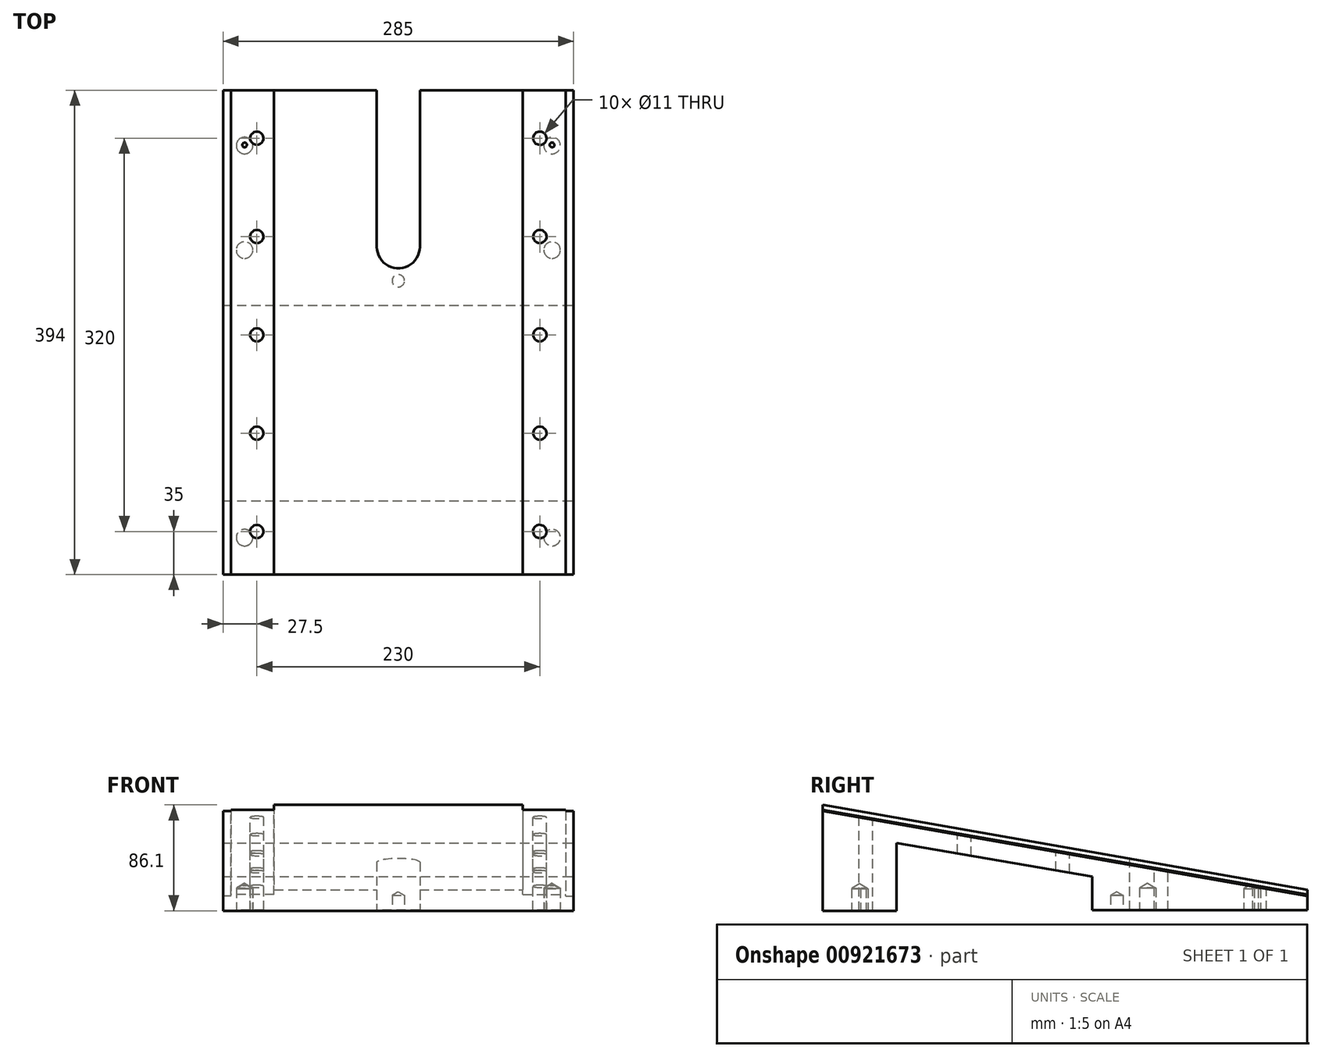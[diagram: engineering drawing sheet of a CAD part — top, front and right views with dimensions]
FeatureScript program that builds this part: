
annotation { "Feature Type Name" : "Feature", "Feature Type Description" : "" }
export const myFeature = defineFeature(function(context is Context, id is Id, definition is map)
    precondition{}
    {
        {
            var Q0;
            Q0=qCreatedBy(makeId("Right.planeOp"),FACE);
            var sketch = newSketch(context, id + "F0", { "sketchPlane" : qUnion([Q0])});
            skLineSegment(sketch, "E0", {"start": v(0, 86.1) * mm, "end": v(0, 65.8) * mm});
            skLineSegment(sketch, "E1", {"start": v(0, 65.8) * mm, "end": v(0, 0) * mm});
            skLineSegment(sketch, "E2", {"start": v(0, 0) * mm, "end": v(60, 0) * mm});
            skLineSegment(sketch, "E3", {"start": v(394, 0.48) * mm, "end": v(394, 17.08) * mm});
            skLineSegment(sketch, "E4", {"start": v(0, 86.1) * mm, "end": v(394, 17.08) * mm});
            skLineSegment(sketch, "E5", {"start": v(60, 0) * mm, "end": v(60, 55.2) * mm});
            skLineSegment(sketch, "E6", {"start": v(394, 0.48) * mm, "end": v(219, 0.48) * mm});
            skLineSegment(sketch, "E7", {"start": v(219, 0.48) * mm, "end": v(219, 27.68) * mm});
            skLineSegment(sketch, "E8", {"start": v(0, 65.8) * mm, "end": v(60, 55.2) * mm});
            skLineSegment(sketch, "E9", {"start": v(60, 55.2) * mm, "end": v(219, 27.68) * mm});
            skPoint(sketch, "E10.start.orphan", {"position": v(249, 0.48) * mm});
            skPoint(sketch, "E11", {"position": v(40.39, 79.03) * mm});
            skPoint(sketch, "E12", {"position": v(119.19, 65.22) * mm});
            skPoint(sketch, "E13", {"position": v(197.99, 51.42) * mm});
            skPoint(sketch, "E14", {"position": v(276.79, 37.61) * mm});
            skPoint(sketch, "E15", {"position": v(355.59, 23.8) * mm});
            skSolve(sketch);
        }
        {
            var Q0;
            {var subQ0=sQuery(id+"F0.wireOp",EDGE,"E1");Q0=makeQuery(id+"F0.imprint","IMPRINT",FACE,{"disambiguationData":[TD([[makeQuery(id+"F0.imprint","IMPRINT",EDGE,{"derivedFrom":subQ0}),1.0]])]});}
            var Q1;
            {var subQ3=sQuery(id+"F0.wireOp",EDGE,"E0");Q1=makeQuery(id+"F0.imprint","IMPRINT",FACE,{"disambiguationData":[TD([[makeQuery(id+"F0.imprint","IMPRINT",EDGE,{"derivedFrom":subQ3}),1.0]])]});}
            var Q2;
            {var subQ0=sQuery(id+"F0.wireOp",EDGE,"E7");Q2=makeQuery(id+"F0.imprint","IMPRINT",FACE,{"disambiguationData":[TD([[makeQuery(id+"F0.imprint","IMPRINT",EDGE,{"derivedFrom":subQ0}),-1.0]])]});}
            var Q3;
            {var subQ0=sQuery(id+"F0.wireOp",EDGE,"E6");var subQ1=sQuery(id+"F0.wireOp",EDGE,"0UA3Y2bc-zSIp-0L5M-hBtJ-KGsreEd9ITGh");var subQ2=makeQuery(id+"F0.imprint","INTERSECT",VERTEX,{"derivedFrom":[subQ1,subQ0]});Q3=makeQuery(id+"F0.imprint","IMPRINT",FACE,{"disambiguationData":[TD([[makeQuery(id+"F0.imprint","IMPRINT",EDGE,{"disambiguationData":[TD([[subQ2,1.0]])],"derivedFrom":subQ1}),-1.0]])]});}
            var Q4;
            {var subQ1=sQuery(id+"F0.wireOp",EDGE,"E3");Q4=makeQuery(id+"F0.imprint","IMPRINT",FACE,{"disambiguationData":[TD([[makeQuery(id+"F0.imprint","IMPRINT",EDGE,{"derivedFrom":subQ1}),1.0]])]});}
            extrude(context, id + "F1", {"entities" : qUnion([Q0, Q1, Q2, Q3, Q4]), "oppositeDirection" : true, "depth" : 285 * mm, "offsetDistance" : 25 * mm});
        }
        {
            var Q0;
            Q0=makeQuery(id+"F1.opExtrude","CAP_FACE",FACE,{"disambiguationData":[OSD([sQuery(id+"F0.wireOp",EDGE,"E0"),sQuery(id+"F0.wireOp",EDGE,"E1"),sQuery(id+"F0.wireOp",EDGE,"E2"),sQuery(id+"F0.wireOp",EDGE,"E3"),sQuery(id+"F0.wireOp",EDGE,"E4"),sQuery(id+"F0.wireOp",EDGE,"0UA3Y2bc-zSIp-0L5M-hBtJ-KGsreEd9ITGh"),sQuery(id+"F0.wireOp",EDGE,"E5"),sQuery(id+"F0.wireOp",EDGE,"E6"),sQuery(id+"F0.wireOp",EDGE,"E7")])],"isStart":true});
            var sketch = newSketch(context, id + "F2", { "sketchPlane" : qUnion([Q0])});
            skLineSegment(sketch, "E16", {"start": v(0, 86.1) * mm, "end": v(0, 82.1) * mm});
            skLineSegment(sketch, "E17", {"start": v(0, 82.1) * mm, "end": v(394, 13.08) * mm});
            skLineSegment(sketch, "E18", {"start": v(394, 13.08) * mm, "end": v(394, 17.08) * mm});
            skLineSegment(sketch, "E19", {"start": v(394, 17.08) * mm, "end": v(0, 86.1) * mm});
            skSolve(sketch);
        }
        {
            var Q0;
            Q0=makeQuery(id+"F2.imprint","IMPRINT",FACE,{"disambiguationData":[TD([[makeQuery(id+"F2.imprint","IMPRINT",EDGE,{"derivedFrom":sQuery(id+"F2.wireOp",EDGE,"E16")}),1.0]])]});
            extrude(context, id + "F3", {"entities" : qUnion([Q0]), "operationType" : NewBodyOperationType.REMOVE, "oppositeDirection" : true, "depth" : 41.5 * mm, "offsetDistance" : 25 * mm});
        }
        {
            var Q0;
            Q0=makeQuery(id+"F1.opExtrude","CAP_FACE",FACE,{"disambiguationData":[OSD([sQuery(id+"F0.wireOp",EDGE,"E0"),sQuery(id+"F0.wireOp",EDGE,"E1"),sQuery(id+"F0.wireOp",EDGE,"E2"),sQuery(id+"F0.wireOp",EDGE,"E3"),sQuery(id+"F0.wireOp",EDGE,"E4"),sQuery(id+"F0.wireOp",EDGE,"0UA3Y2bc-zSIp-0L5M-hBtJ-KGsreEd9ITGh"),sQuery(id+"F0.wireOp",EDGE,"E5"),sQuery(id+"F0.wireOp",EDGE,"E6"),sQuery(id+"F0.wireOp",EDGE,"E7")])],"isStart":true});
            var sketch = newSketch(context, id + "F4", { "sketchPlane" : qUnion([Q0])});
            skLineSegment(sketch, "E20", {"start": v(0, 82.1) * mm, "end": v(0, 81.1) * mm});
            skLineSegment(sketch, "E21", {"start": v(0, 81.1) * mm, "end": v(394, 12.08) * mm});
            skLineSegment(sketch, "E22", {"start": v(394, 12.08) * mm, "end": v(394, 13.08) * mm});
            skLineSegment(sketch, "E23", {"start": v(0, 82.1) * mm, "end": v(394, 13.08) * mm});
            skSolve(sketch);
        }
        {
            var Q0;
            Q0=makeQuery(id+"F4.imprint","IMPRINT",FACE,{"disambiguationData":[TD([[makeQuery(id+"F4.imprint","IMPRINT",EDGE,{"derivedFrom":sQuery(id+"F4.wireOp",EDGE,"E20")}),1.0]])]});
            extrude(context, id + "F5", {"entities" : qUnion([Q0]), "operationType" : NewBodyOperationType.REMOVE, "oppositeDirection" : true, "depth" : 6.5 * mm, "offsetDistance" : 25 * mm});
        }
        {
            var Q0;
            Q0=makeQuery(id+"F1.opExtrude","CAP_FACE",FACE,{"disambiguationData":[OSD([sQuery(id+"F0.wireOp",EDGE,"E0"),sQuery(id+"F0.wireOp",EDGE,"E1"),sQuery(id+"F0.wireOp",EDGE,"E2"),sQuery(id+"F0.wireOp",EDGE,"E3"),sQuery(id+"F0.wireOp",EDGE,"E4"),sQuery(id+"F0.wireOp",EDGE,"0UA3Y2bc-zSIp-0L5M-hBtJ-KGsreEd9ITGh"),sQuery(id+"F0.wireOp",EDGE,"E5"),sQuery(id+"F0.wireOp",EDGE,"E6"),sQuery(id+"F0.wireOp",EDGE,"E7")])],"isStart":false});
            var sketch = newSketch(context, id + "F6", { "sketchPlane" : qUnion([Q0])});
            skLineSegment(sketch, "E24", {"start": v(-394, 17.08) * mm, "end": v(-394, 13.08) * mm});
            skLineSegment(sketch, "E25", {"start": v(-394, 13.08) * mm, "end": v(-394, 12.08) * mm});
            skLineSegment(sketch, "E26", {"start": v(0, 86.1) * mm, "end": v(0, 82.1) * mm});
            skLineSegment(sketch, "E27", {"start": v(0, 82.1) * mm, "end": v(0, 81.1) * mm});
            skLineSegment(sketch, "E28", {"start": v(0, 86.1) * mm, "end": v(-394, 17.08) * mm});
            skLineSegment(sketch, "E29", {"start": v(-394, 13.08) * mm, "end": v(0, 82.1) * mm});
            skLineSegment(sketch, "E30", {"start": v(0, 81.1) * mm, "end": v(-394, 12.08) * mm});
            skSolve(sketch);
        }
        {
            var Q0;
            Q0=makeQuery(id+"F6.imprint","IMPRINT",FACE,{"disambiguationData":[TD([[makeQuery(id+"F6.imprint","IMPRINT",EDGE,{"derivedFrom":sQuery(id+"F6.wireOp",EDGE,"E24")}),-1.0]])]});
            extrude(context, id + "F7", {"entities" : qUnion([Q0]), "operationType" : NewBodyOperationType.REMOVE, "oppositeDirection" : true, "depth" : 41.5 * mm, "offsetDistance" : 25 * mm});
        }
        {
            var Q0;
            Q0=makeQuery(id+"F6.imprint","IMPRINT",FACE,{"disambiguationData":[TD([[makeQuery(id+"F6.imprint","IMPRINT",EDGE,{"derivedFrom":sQuery(id+"F6.wireOp",EDGE,"E25")}),-1.0]])]});
            extrude(context, id + "F8", {"entities" : qUnion([Q0]), "operationType" : NewBodyOperationType.REMOVE, "oppositeDirection" : true, "depth" : 6.5 * mm, "offsetDistance" : 25 * mm});
        }
        {
            var Q0;
            Q0=makeQuery(id+"F1.opExtrude","SWEPT_FACE",FACE,{"disambiguationData":[OSD([sQuery(id+"F0.wireOp",EDGE,"E4")])]});
            var sketch = newSketch(context, id + "F9", { "sketchPlane" : qUnion([Q0])});
            skSolve(sketch);
        }
        {
            var Q0;
            Q0=makeQuery(id+"F9.imprint","IMPRINT",FACE,{"disambiguationData":[TD([[makeQuery(id+"F9.imprint","IMPRINT",EDGE,{"derivedFrom":makeQuery(id+"F3.boolean.opBoolean","COPY",EDGE,{"derivedFrom":makeQuery(id+"F3.opExtrude","CAP_EDGE",EDGE,{"disambiguationData":[OSD([sQuery(id+"F2.wireOp",EDGE,"E19")])],"isStart":false})})}),1.0]])]});
            var sketch = newSketch(context, id + "F10", { "sketchPlane" : qUnion([Q0])});
            skSolve(sketch);
        }
        {
            var Q0;
            Q0=qCreatedBy(makeId("Top.planeOp"),FACE);
            cPlane(context, id + "F11", {"entities" : qUnion([Q0]), "cplaneType" : CPlaneType.OFFSET, "offset" : 86.1 * mm, "width" : 150 * mm, "height" : 150 * mm});
        }
        {
            var Q0;
            Q0=qCreatedBy(id+"F11.planeOp",FACE);
            var sketch = newSketch(context, id + "F12", { "sketchPlane" : qUnion([Q0])});
            skLineSegment(sketch, "E31", {"start": v(-257.5, 394) * mm, "end": v(-257.5, -6) * mm, "construction": true});
            skLineSegment(sketch, "E32", {"start": v(-27.5, 394) * mm, "end": v(-27.5, -70.85) * mm, "construction": true});
            skPoint(sketch, "E33", {"position": v(-257.5, 355) * mm});
            skPoint(sketch, "E34", {"position": v(-257.5, 275) * mm});
            skPoint(sketch, "E35", {"position": v(-257.5, 195) * mm});
            skPoint(sketch, "E36", {"position": v(-257.5, -6) * mm});
            skPoint(sketch, "E37", {"position": v(-27.5, 355) * mm});
            skPoint(sketch, "E38", {"position": v(-27.5, 275) * mm});
            skPoint(sketch, "E39", {"position": v(-27.5, 195) * mm});
            skPoint(sketch, "E40", {"position": v(-27.5, 115) * mm});
            skPoint(sketch, "E41", {"position": v(-27.5, 35) * mm});
            skLineSegment(sketch, "E42.0.0", {"start": v(-243.5, 394) * mm, "end": v(-278.5, 394) * mm});
            skLineSegment(sketch, "E42.0.1", {"start": v(-278.5, 394) * mm, "end": v(-278.5, 0) * mm});
            skLineSegment(sketch, "E42.0.2", {"start": v(-278.5, 0) * mm, "end": v(-243.5, 0) * mm});
            skLineSegment(sketch, "E42.0.3", {"start": v(-243.5, 0) * mm, "end": v(-243.5, 394) * mm});
            skPoint(sketch, "E43", {"position": v(-257.5, 115) * mm});
            skPoint(sketch, "E44", {"position": v(-257.5, 35) * mm});
            skLineSegment(sketch, "E45.0", {"start": v(-285, 0) * mm, "end": v(0, 0) * mm, "construction": true});
            skSolve(sketch);
        }
        {
            var Q0;
            Q0=sQuery(id+"F12.wireOp",VERTEX,"E33");
            var Q1;
            Q1=sQuery(id+"F12.wireOp",VERTEX,"E34");
            var Q2;
            Q2=sQuery(id+"F12.wireOp",VERTEX,"E35");
            var Q3;
            Q3=sQuery(id+"F12.wireOp",VERTEX,"E37");
            var Q4;
            Q4=sQuery(id+"F12.wireOp",VERTEX,"E38");
            var Q5;
            Q5=sQuery(id+"F12.wireOp",VERTEX,"E39");
            var Q6;
            Q6=sQuery(id+"F12.wireOp",VERTEX,"E40");
            var Q7;
            Q7=sQuery(id+"F12.wireOp",VERTEX,"E41");
            var Q8;
            Q8=sQuery(id+"F12.wireOp",VERTEX,"8ee47a5b-37d2-4881-83f4-5071e9de7b0a");
            var Q9;
            Q9=sQuery(id+"F12.wireOp",VERTEX,"E43");
            var Q10;
            Q10=sQuery(id+"F12.wireOp",VERTEX,"E44");
            var Q11;
            Q11=makeQuery(id+"F1.opExtrude","SWEPT_BODY",BODY,{"disambiguationData":[OSD([sQuery(id+"F0.wireOp",EDGE,"E0"),sQuery(id+"F0.wireOp",EDGE,"E1"),sQuery(id+"F0.wireOp",EDGE,"E2"),sQuery(id+"F0.wireOp",EDGE,"E3"),sQuery(id+"F0.wireOp",EDGE,"E4"),sQuery(id+"F0.wireOp",EDGE,"E5"),sQuery(id+"F0.wireOp",EDGE,"E6"),sQuery(id+"F0.wireOp",EDGE,"E7"),sQuery(id+"F0.wireOp",EDGE,"E9")])]});
            hole(context, id + "F13", {"style" : HoleStyle.SIMPLE, "endStyle" : HoleEndStyle.THROUGH, "standardTappedOrClearance" : lookupTablePath({ "fit" : "Normal", "standard" : "ISO", "size" : "M10", "type" : "Clearance" }), "standardBlindInLast" : lookupTablePath({ "fit" : "Normal", "standard" : "ISO", "size" : "M10", "type" : "Clearance" }), "holeDiameter" : 11 * mm, "majorDiameter" : 5 * mm, "isTappedThrough" : true, "tappedDepth" : 12 * mm, "tapClearance" : 3, "locations" : qUnion([Q0, Q1, Q2, Q3, Q4, Q5, Q6, Q7, Q8, Q9, Q10]), "scope" : qUnion([Q11])});
        }
        {
            var Q0;
            Q0=makeQuery(id+"F1.opExtrude","SWEPT_FACE",FACE,{"disambiguationData":[OSD([sQuery(id+"F0.wireOp",EDGE,"E2")])]});
            var sketch = newSketch(context, id + "F14", { "sketchPlane" : qUnion([Q0])});
            skLineSegment(sketch, "E46.0", {"start": v(-285, 0) * mm, "end": v(0, 0) * mm});
            skLineSegment(sketch, "E47", {"start": v(-142.5, 0) * mm, "end": v(-142.5, -475.57) * mm, "construction": true});
            skLineSegment(sketch, "E48", {"start": v(-142.5, 0) * mm, "end": v(-17.5, 0) * mm, "construction": true});
            skLineSegment(sketch, "E49", {"start": v(-17.5, 0) * mm, "end": v(-17.5, -415.07) * mm, "construction": true});
            skPoint(sketch, "E50", {"position": v(-17.5, -30) * mm});
            skPoint(sketch, "E51", {"position": v(-17.5, -264) * mm});
            skLineSegment(sketch, "E52", {"start": v(-142.5, 0) * mm, "end": v(-267.5, 0) * mm, "construction": true});
            skLineSegment(sketch, "E53", {"start": v(-267.5, 0) * mm, "end": v(-267.5, -443.76) * mm, "construction": true});
            skPoint(sketch, "E54", {"position": v(-267.5, -30) * mm});
            skPoint(sketch, "E55", {"position": v(-267.5, -264) * mm});
            skPoint(sketch, "E56", {"position": v(-17.5, -349) * mm});
            skLineSegment(sketch, "E57.0", {"start": v(-285, -394) * mm, "end": v(0, -394) * mm});
            skPoint(sketch, "E58", {"position": v(-267.5, -349) * mm});
            skSolve(sketch);
        }
        {
            var Q0;
            Q0=sQuery(id+"F14.wireOp",VERTEX,"E56");
            var Q1;
            Q1=sQuery(id+"F14.wireOp",VERTEX,"E51");
            var Q2;
            Q2=sQuery(id+"F14.wireOp",VERTEX,"E50");
            var Q3;
            Q3=sQuery(id+"F14.wireOp",VERTEX,"E54");
            var Q4;
            Q4=sQuery(id+"F14.wireOp",VERTEX,"E55");
            var Q5;
            Q5=sQuery(id+"F14.wireOp",VERTEX,"E58");
            var Q6;
            Q6=makeQuery(id+"F1.opExtrude","SWEPT_BODY",BODY,{"disambiguationData":[OSD([sQuery(id+"F0.wireOp",EDGE,"E0"),sQuery(id+"F0.wireOp",EDGE,"E1"),sQuery(id+"F0.wireOp",EDGE,"E2"),sQuery(id+"F0.wireOp",EDGE,"E3"),sQuery(id+"F0.wireOp",EDGE,"E4"),sQuery(id+"F0.wireOp",EDGE,"E5"),sQuery(id+"F0.wireOp",EDGE,"E6"),sQuery(id+"F0.wireOp",EDGE,"E7"),sQuery(id+"F0.wireOp",EDGE,"E9")])]});
            hole(context, id + "F15", {"style" : HoleStyle.SIMPLE, "endStyle" : HoleEndStyle.BLIND, "standardTappedOrClearance" : lookupTablePath({ "fit" : "Normal", "standard" : "ISO", "size" : "M12", "type" : "Clearance" }), "standardBlindInLast" : lookupTablePath({ "fit" : "Normal", "standard" : "ISO", "size" : "M12", "type" : "Clearance" }), "holeDiameter" : 13.5 * mm, "majorDiameter" : 5 * mm, "holeDepth" : 18 * mm, "isTappedThrough" : true, "tappedDepth" : 12 * mm, "tapClearance" : 3, "locations" : qUnion([Q0, Q1, Q2, Q3, Q4, Q5]), "scope" : qUnion([Q6])});
        }
        {
            var Q0;
            Q0=makeQuery(id+"F1.opExtrude","SWEPT_FACE",FACE,{"disambiguationData":[OSD([sQuery(id+"F0.wireOp",EDGE,"E6")])]});
            var sketch = newSketch(context, id + "F16", { "sketchPlane" : qUnion([Q0])});
            skLineSegment(sketch, "E59.top", {"start": v(-125, -394) * mm, "end": v(-160, -394) * mm});
            skLineSegment(sketch, "E59.left", {"start": v(-125, -266.5) * mm, "end": v(-125, -394) * mm});
            skLineSegment(sketch, "E59.right", {"start": v(-160, -266.5) * mm, "end": v(-160, -394) * mm});
            skArc(sketch, "E60", {"start": v(-125, -266.5) * mm, "mid": v(-142.5, -249) * mm, "end": v(-160, -266.5) * mm});
            skPoint(sketch, "E61.0", {"position": v(-142.5, 0) * mm});
            skSolve(sketch);
        }
        {
            var Q0;
            Q0=makeQuery(id+"F16.imprint","IMPRINT",FACE,{"disambiguationData":[TD([[makeQuery(id+"F16.imprint","IMPRINT",EDGE,{"derivedFrom":sQuery(id+"F16.wireOp",EDGE,"E59.top")}),1.0]])]});
            extrude(context, id + "F17", {"entities" : qUnion([Q0]), "operationType" : NewBodyOperationType.REMOVE, "endBound" : BoundingType.THROUGH_ALL, "oppositeDirection" : true, "depth" : 25 * mm, "offsetDistance" : 25 * mm});
        }
        {
            var Q0;
            Q0=makeQuery(id+"F1.opExtrude","SWEPT_FACE",FACE,{"disambiguationData":[OSD([sQuery(id+"F0.wireOp",EDGE,"E6")])]});
            var sketch = newSketch(context, id + "F18", { "sketchPlane" : qUnion([Q0])});
            skArc(sketch, "E62.0", {"start": v(-22, -35.03) * mm, "mid": v(-32.42, -37.46) * mm, "end": v(-24.22, -30.58) * mm});
            skPoint(sketch, "E63", {"position": v(-142.5, -239) * mm});
            skPoint(sketch, "E63.positionSnap0", {"position": v(-142.5, -249) * mm});
            skSolve(sketch);
        }
        {
            var Q0;
            Q0=sQuery(id+"F18.wireOp",VERTEX,"E63");
            var Q1;
            Q1=makeQuery(id+"F1.opExtrude","SWEPT_BODY",BODY,{"disambiguationData":[OSD([sQuery(id+"F0.wireOp",EDGE,"E0"),sQuery(id+"F0.wireOp",EDGE,"E1"),sQuery(id+"F0.wireOp",EDGE,"E2"),sQuery(id+"F0.wireOp",EDGE,"E3"),sQuery(id+"F0.wireOp",EDGE,"E4"),sQuery(id+"F0.wireOp",EDGE,"E5"),sQuery(id+"F0.wireOp",EDGE,"E6"),sQuery(id+"F0.wireOp",EDGE,"E7"),sQuery(id+"F0.wireOp",EDGE,"E9")])]});
            hole(context, id + "F19", {"style" : HoleStyle.SIMPLE, "endStyle" : HoleEndStyle.BLIND, "holeDiameter" : 10 * mm, "majorDiameter" : 5 * mm, "holeDepth" : 12 * mm, "isTappedThrough" : true, "tappedDepth" : 12 * mm, "tapClearance" : 3, "locations" : qUnion([Q0]), "scope" : qUnion([Q1])});
        }
    });
